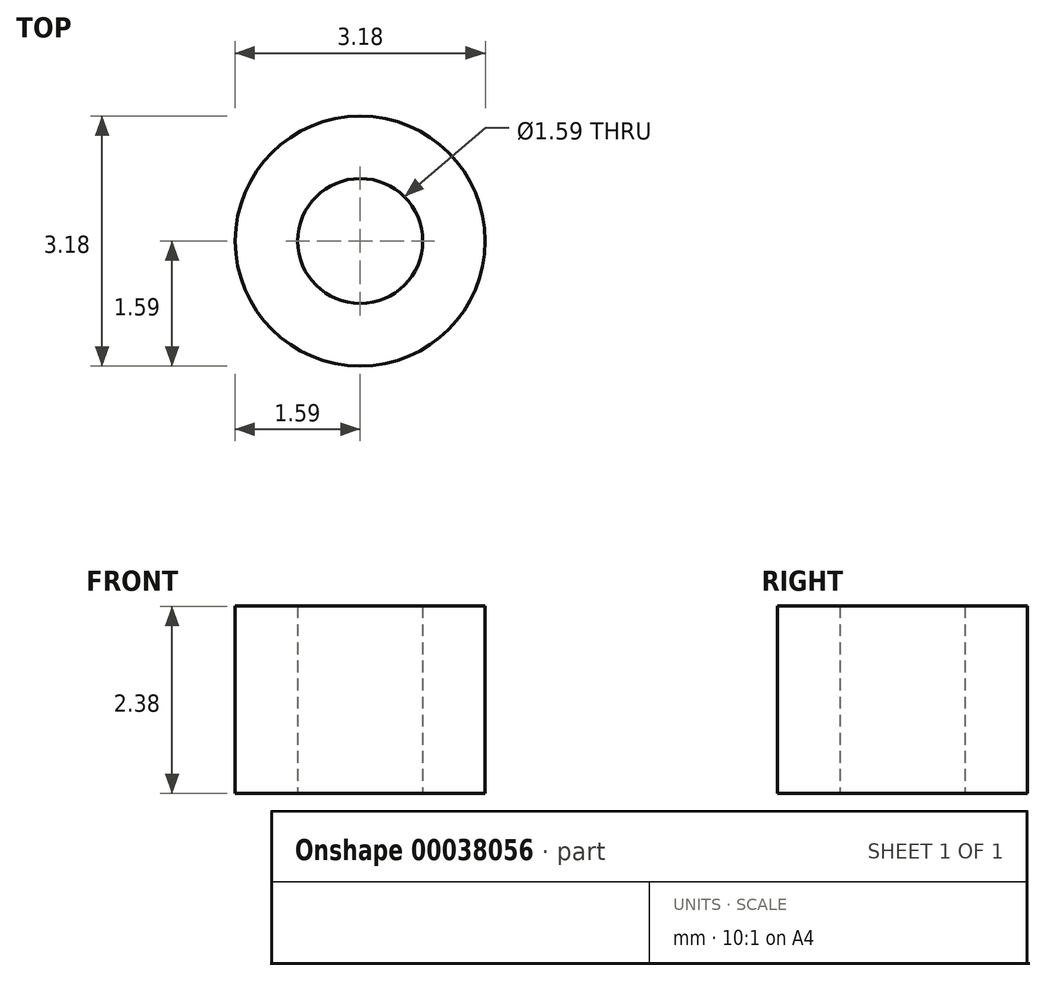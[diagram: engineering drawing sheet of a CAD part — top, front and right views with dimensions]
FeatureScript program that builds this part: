
annotation { "Feature Type Name" : "Feature", "Feature Type Description" : "" }
export const myFeature = defineFeature(function(context is Context, id is Id, definition is map)
    precondition{}
    {
        {
            var Q0;
            Q0=qCreatedBy(makeId("Top.planeOp"),FACE);
            var sketch = newSketch(context, id + "F0", { "sketchPlane" : qUnion([Q0])});
            skCircle(sketch, "E0", {"center": v(0, 0) * mm, "radius": 1.59 * mm});
            skCircle(sketch, "E1", {"center": v(0, 0) * mm, "radius": 0.8 * mm});
            skSolve(sketch);
        }
        {
            var Q0;
            Q0 = qSketchRegion(id + "F0", true);
            extrude(context, id + "F1", {"entities" : qUnion([Q0]), "depth" : 2.38 * mm});
        }
    });
